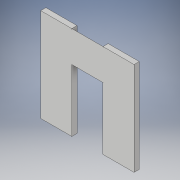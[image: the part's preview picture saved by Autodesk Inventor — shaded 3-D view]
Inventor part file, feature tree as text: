
AUTODESK INVENTOR PART (.ipt)
format: ipt  version: 2017 (Build 210142000, 142)  size: 122,368 bytes
history: native  units: in
note: dims shown in document units (in); Inventor stores cm internally (conversion verified against a paired STEP export)
features: extrude x5, sketch x5
ambient origin geometry x8: Origin, YZ Plane, XZ Plane, XY Plane, X Axis, Y Axis, Z Axis, Center Point
bodies: Solid1 (feature_tree)
feature tree (10):
  extrude  "Extrusion1"  Depth=18.0in
  extrude  "Extrusion2"  Depth=6.0in
  extrude  "Extrusion3"  Depth=6.0in TaperAngle=0.0deg
  extrude  "Extrusion4"  Depth=12.0in TaperAngle=0.0deg
  extrude  "Extrusion5"  [1 undecoded]
  sketch  "Sketch1"  dims[d0=18.0in d1=18.0in]
  sketch  "Sketch2"  dims[d2=1.0in d3=0.0in d4=6.0in]
  sketch  "Sketch3"  dims[d5=18.0in d6=0.0in d7=6.0in d8=0.0in]
  sketch  "Sketch4"  dims[d9=6.0in d10=0.0in d11=12.0in d12=0.0in]
  sketch  "Sketch5"
note: 1 required parameter value undecoded (feature->parameter linkage not recoverable at this tier; creation-order binding heuristic only, values carry confidence <= 0.55)
